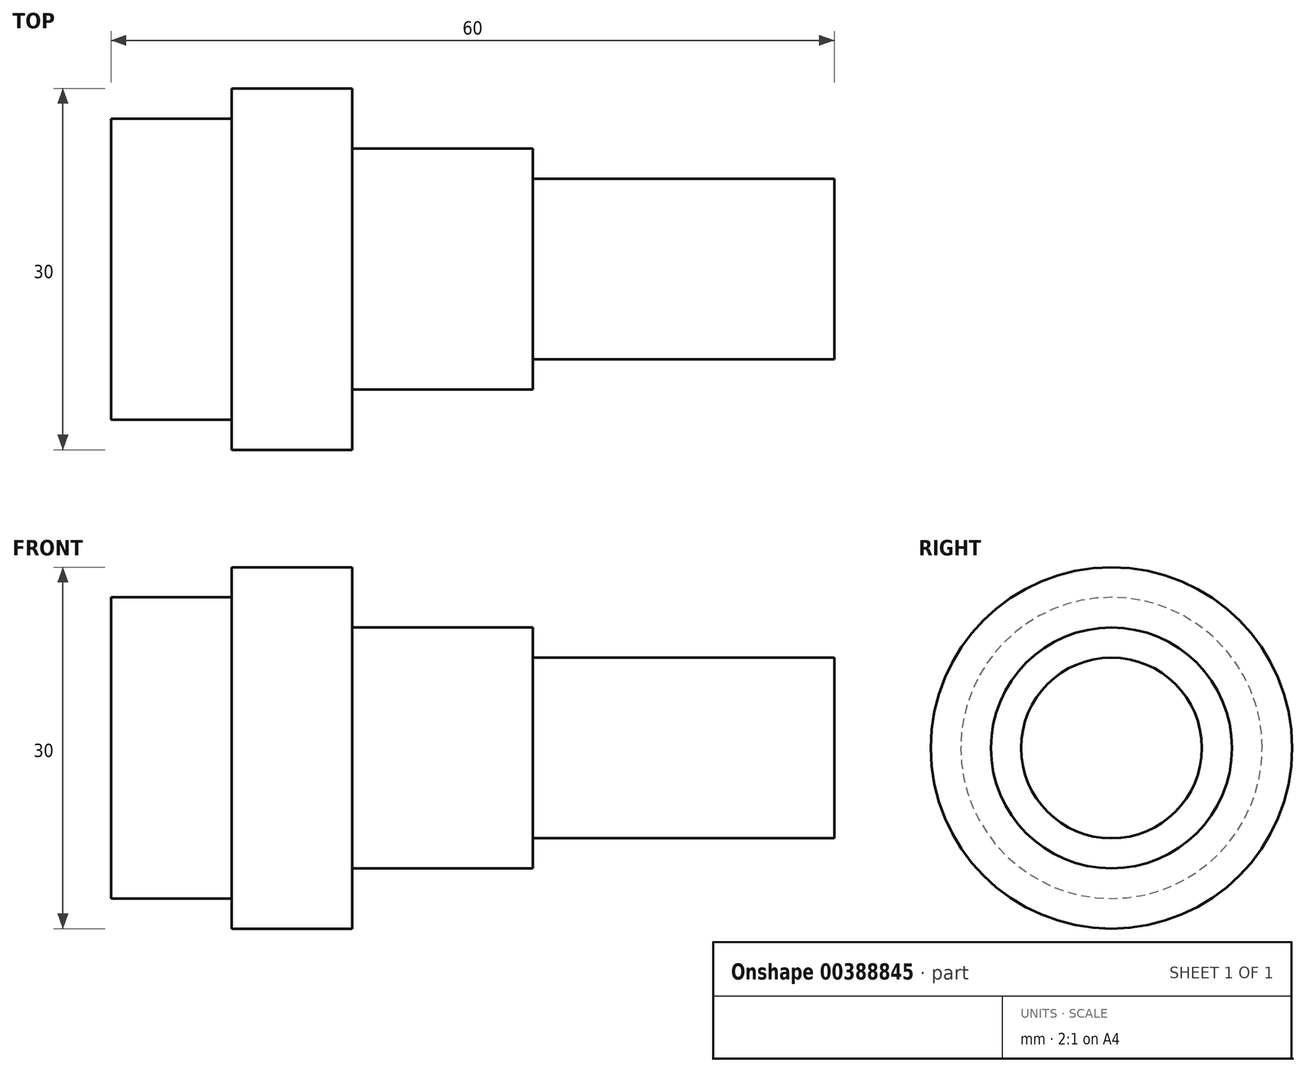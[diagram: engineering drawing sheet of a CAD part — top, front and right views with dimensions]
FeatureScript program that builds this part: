
annotation { "Feature Type Name" : "Feature", "Feature Type Description" : "" }
export const myFeature = defineFeature(function(context is Context, id is Id, definition is map)
    precondition{}
    {
        {
            var Q0;
            Q0=qCreatedBy(makeId("Top.planeOp"),FACE);
            var sketch = newSketch(context, id + "F0", { "sketchPlane" : qUnion([Q0])});
            skLineSegment(sketch, "E0", {"start": v(0, 0) * mm, "end": v(0, 7.5) * mm});
            skLineSegment(sketch, "E1", {"start": v(0, 7.5) * mm, "end": v(-25, 7.5) * mm});
            skLineSegment(sketch, "E2", {"start": v(-25, 7.5) * mm, "end": v(-25, 10) * mm});
            skLineSegment(sketch, "E3", {"start": v(-25, 10) * mm, "end": v(-40, 10) * mm});
            skLineSegment(sketch, "E4", {"start": v(-40, 10) * mm, "end": v(-40, 15) * mm});
            skLineSegment(sketch, "E5", {"start": v(-40, 15) * mm, "end": v(-50, 15) * mm});
            skLineSegment(sketch, "E6", {"start": v(-50, 15) * mm, "end": v(-50, 12.5) * mm});
            skLineSegment(sketch, "E7", {"start": v(-50, 12.5) * mm, "end": v(-60, 12.5) * mm});
            skLineSegment(sketch, "E8", {"start": v(-60, 12.5) * mm, "end": v(-60, 0) * mm});
            skLineSegment(sketch, "E9", {"start": v(-60, 0) * mm, "end": v(0, 0) * mm});
            skLineSegment(sketch, "E10", {"start": v(-71.67, 0) * mm, "end": v(11.3, 0) * mm, "construction": true});
            skSolve(sketch);
        }
        {
            var Q0;
            Q0 = qSketchRegion(id + "F0", true);
            var Q1;
            Q1=sQuery(id+"F0.wireOp",EDGE,"E9");
            revolve(context, id + "F1", {"entities" : qUnion([Q0]), "axis" : qUnion([Q1]), "revolveType" : RevolveType.FULL});
        }
    });
